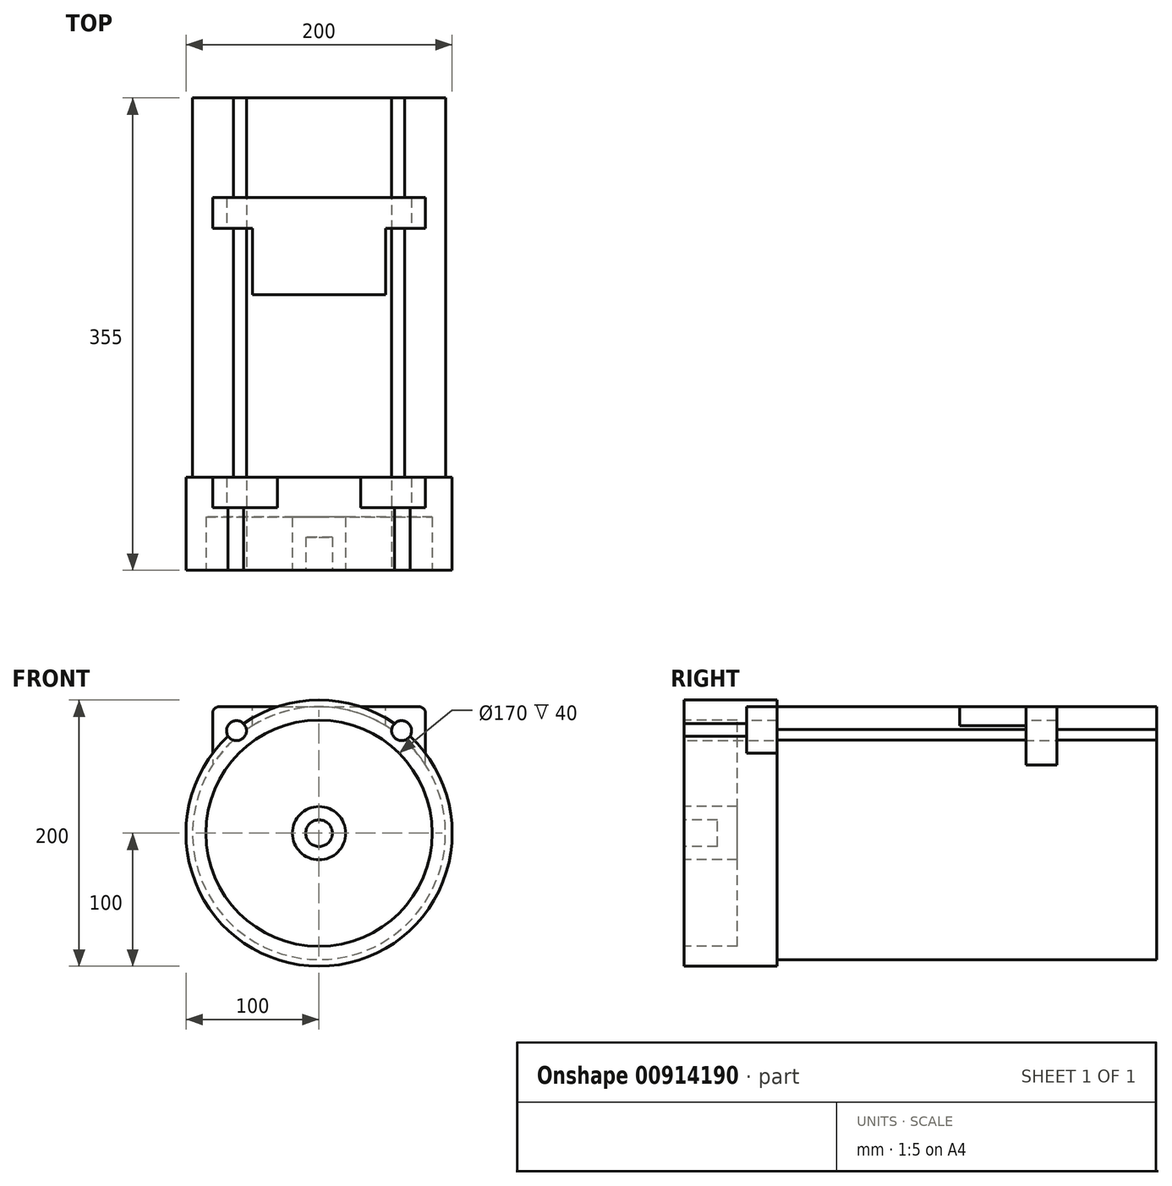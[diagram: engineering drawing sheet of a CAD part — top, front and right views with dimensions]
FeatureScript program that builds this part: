
annotation { "Feature Type Name" : "Feature", "Feature Type Description" : "" }
export const myFeature = defineFeature(function(context is Context, id is Id, definition is map)
    precondition{}
    {
        {
            var Q0;
            Q0=qCreatedBy(makeId("Front.planeOp"),FACE);
            var sketch = newSketch(context, id + "F0", { "sketchPlane" : qUnion([Q0])});
            skCircle(sketch, "E0", {"center": v(0, 0) * mm, "radius": 95 * mm});
            skSolve(sketch);
        }
        {
            var Q0;
            Q0 = qSketchRegion(id + "F0", true);
            extrude(context, id + "F1", {"entities" : qUnion([Q0]), "depth" : 355 * mm, "offsetDistance" : 25 * mm});
        }
        {
            var Q0;
            Q0=makeQuery(id+"F1.opExtrude","CAP_FACE",FACE,{"disambiguationData":[OSD([sQuery(id+"F0.wireOp",EDGE,"E0")])],"isStart":false});
            var sketch = newSketch(context, id + "F2", { "sketchPlane" : qUnion([Q0])});
            skLineSegment(sketch, "E1.top", {"start": v(80, 95) * mm, "end": v(46.44, 95) * mm});
            skPoint(sketch, "E1.middle", {"position": v(0, 0) * mm});
            skLineSegment(sketch, "E2.trimOffspring", {"start": v(-80, 50) * mm, "end": v(-80, 95) * mm});
            skLineSegment(sketch, "E3.trimOffspring", {"start": v(80, 50) * mm, "end": v(80, 95) * mm});
            skLineSegment(sketch, "E4.trimOffspring", {"start": v(-46.44, 95) * mm, "end": v(-80, 95) * mm});
            skLineSegment(sketch, "E5", {"start": v(-80, 50) * mm, "end": v(80, 50) * mm});
            skLineSegment(sketch, "E6", {"start": v(-46.44, 95) * mm, "end": v(46.44, 95) * mm});
            skLineSegment(sketch, "E7", {"start": v(0, 0) * mm, "end": v(0, 50) * mm, "construction": true});
            skSolve(sketch);
        }
        {
            var Q0;
            Q0 = qSketchRegion(id + "F2", true);
            extrude(context, id + "F3", {"entities" : qUnion([Q0]), "operationType" : NewBodyOperationType.ADD, "oppositeDirection" : true, "depth" : 70 * mm, "offsetDistance" : 25 * mm});
        }
        {
            var Q0;
            Q0=makeQuery(id+"F3.boolean.opBoolean","MERGE",FACE,{"derivedFrom":[makeQuery(id+"F1.opExtrude","CAP_FACE",FACE,{"disambiguationData":[OSD([sQuery(id+"F0.wireOp",EDGE,"E0")])],"isStart":false}),makeQuery(id+"F3.opExtrude","CAP_FACE",FACE,{"disambiguationData":[OSD([sQuery(id+"F2.wireOp",EDGE,"lusTuei3-iRUz-YuGS-ICs9-9Co0ldXmLETs"),sQuery(id+"F2.wireOp",EDGE,"E1.bottom"),sQuery(id+"F2.wireOp",EDGE,"E1.top"),sQuery(id+"F2.wireOp",EDGE,"E1.left"),sQuery(id+"F2.wireOp",EDGE,"E1.right"),sQuery(id+"F2.wireOp",EDGE,"226f6c96-94c5-4a05-a829-39864204098a.trimOffspring"),sQuery(id+"F2.wireOp",EDGE,"b6210ef0-624a-4716-9d17-52c4b066af3b.trimOffspring"),sQuery(id+"F2.wireOp",EDGE,"a472ba7a-83c2-47c1-b5ba-f65e10f710ef.trimOffspring"),sQuery(id+"F2.wireOp",EDGE,"E2.trimOffspring"),sQuery(id+"F2.wireOp",EDGE,"E3.trimOffspring"),sQuery(id+"F2.wireOp",EDGE,"E4.trimOffspring"),sQuery(id+"F2.wireOp",EDGE,"4b05afef-a105-4b7d-babe-68159069cd75.trimOffspring")])],"isStart":true})]});
            var sketch = newSketch(context, id + "F4", { "sketchPlane" : qUnion([Q0])});
            skCircle(sketch, "E8", {"center": v(0, 0) * mm, "radius": 85 * mm});
            skCircle(sketch, "E9", {"center": v(0, 0) * mm, "radius": 20 * mm});
            skSolve(sketch);
        }
        {
            var Q0;
            Q0=makeQuery(id+"F4.imprint","IMPRINT",FACE,{"disambiguationData":[TD([[makeQuery(id+"F4.imprint","IMPRINT",EDGE,{"derivedFrom":sQuery(id+"F4.wireOp",EDGE,"E8")}),1.0]])]});
            extrude(context, id + "F5", {"entities" : qUnion([Q0]), "operationType" : NewBodyOperationType.REMOVE, "oppositeDirection" : true, "depth" : 40 * mm, "offsetDistance" : 25 * mm});
        }
        {
            var Q0;
            Q0=makeQuery(id+"F5.boolean.opBoolean","SPLIT",FACE,{"disambiguationData":[TD([makeQuery(id+"F5.opExtrude","SWEPT_FACE",FACE,{"disambiguationData":[OSD([sQuery(id+"F4.wireOp",EDGE,"E9")])]})])],"derivedFrom":makeQuery(id+"F3.boolean.opBoolean","MERGE",FACE,{"derivedFrom":[makeQuery(id+"F1.opExtrude","CAP_FACE",FACE,{"disambiguationData":[OSD([sQuery(id+"F0.wireOp",EDGE,"E0")])],"isStart":false}),makeQuery(id+"F3.opExtrude","CAP_FACE",FACE,{"disambiguationData":[OSD([sQuery(id+"F2.wireOp",EDGE,"lusTuei3-iRUz-YuGS-ICs9-9Co0ldXmLETs"),sQuery(id+"F2.wireOp",EDGE,"E1.bottom"),sQuery(id+"F2.wireOp",EDGE,"E1.top"),sQuery(id+"F2.wireOp",EDGE,"E1.left"),sQuery(id+"F2.wireOp",EDGE,"E1.right"),sQuery(id+"F2.wireOp",EDGE,"226f6c96-94c5-4a05-a829-39864204098a.trimOffspring"),sQuery(id+"F2.wireOp",EDGE,"b6210ef0-624a-4716-9d17-52c4b066af3b.trimOffspring"),sQuery(id+"F2.wireOp",EDGE,"a472ba7a-83c2-47c1-b5ba-f65e10f710ef.trimOffspring"),sQuery(id+"F2.wireOp",EDGE,"E2.trimOffspring"),sQuery(id+"F2.wireOp",EDGE,"E3.trimOffspring"),sQuery(id+"F2.wireOp",EDGE,"E4.trimOffspring"),sQuery(id+"F2.wireOp",EDGE,"4b05afef-a105-4b7d-babe-68159069cd75.trimOffspring")])],"isStart":true})]})});
            var sketch = newSketch(context, id + "F6", { "sketchPlane" : qUnion([Q0])});
            skCircle(sketch, "E10", {"center": v(0, 0) * mm, "radius": 10 * mm});
            skSolve(sketch);
        }
        {
            var Q0;
            Q0 = qSketchRegion(id + "F6", true);
            extrude(context, id + "F7", {"entities" : qUnion([Q0]), "operationType" : NewBodyOperationType.REMOVE, "oppositeDirection" : true, "depth" : 25 * mm, "offsetDistance" : 25 * mm});
        }
        {
            var Q0;
            {var subQ0=sQuery(id+"F2.wireOp",EDGE,"E1.left");var subQ1=sQuery(id+"F2.wireOp",EDGE,"E1.top");var subQ2=sQuery(id+"F2.wireOp",EDGE,"E1.bottom");var subQ3=sQuery(id+"F0.wireOp",EDGE,"E0");var subQ4=sQuery(id+"F2.wireOp",EDGE,"E2.trimOffspring");var subQ5=sQuery(id+"F2.wireOp",EDGE,"E1.right");var subQ6=sQuery(id+"F2.wireOp",EDGE,"E3.trimOffspring");var subQ7=sQuery(id+"F2.wireOp",EDGE,"E4.trimOffspring");var subQ8=sQuery(id+"F2.wireOp",EDGE,"4b05afef-a105-4b7d-babe-68159069cd75.trimOffspring");Q0=makeQuery(id+"F5.boolean.opBoolean","SPLIT",FACE,{"disambiguationData":[TD([makeQuery(id+"F1.opExtrude","SWEPT_FACE",FACE,{"disambiguationData":[OSD([subQ3])]})])],"derivedFrom":makeQuery(id+"F3.boolean.opBoolean","MERGE",FACE,{"derivedFrom":[makeQuery(id+"F1.opExtrude","CAP_FACE",FACE,{"disambiguationData":[OSD([subQ3])],"isStart":false}),makeQuery(id+"F3.opExtrude","CAP_FACE",FACE,{"disambiguationData":[OSD([sQuery(id+"F2.wireOp",EDGE,"lusTuei3-iRUz-YuGS-ICs9-9Co0ldXmLETs"),subQ2,subQ1,subQ0,subQ5,sQuery(id+"F2.wireOp",EDGE,"226f6c96-94c5-4a05-a829-39864204098a.trimOffspring"),sQuery(id+"F2.wireOp",EDGE,"b6210ef0-624a-4716-9d17-52c4b066af3b.trimOffspring"),sQuery(id+"F2.wireOp",EDGE,"a472ba7a-83c2-47c1-b5ba-f65e10f710ef.trimOffspring"),subQ4,subQ6,subQ7,subQ8])],"isStart":true})]})});}
            var sketch = newSketch(context, id + "F8", { "sketchPlane" : qUnion([Q0])});
            skCircle(sketch, "E11", {"center": v(-62, 77) * mm, "radius": 7.5 * mm});
            skCircle(sketch, "E12.3.0", {"center": v(62, 77) * mm, "radius": 7.5 * mm});
            skPoint(sketch, "E12.center", {"position": v(0, 15) * mm});
            skSolve(sketch);
        }
        {
            var Q0;
            Q0=makeQuery(id+"F2zg9YKfClmn7O4_1.1.F3.boolean.opBoolean","MERGE",FACE,{"derivedFrom":[makeQuery(id+"F1.opExtrude","CAP_FACE",FACE,{"disambiguationData":[OSD([sQuery(id+"F0.wireOp",EDGE,"E0")])],"isStart":true}),makeQuery(id+"F2zg9YKfClmn7O4_1.1.F3.opExtrude","CAP_FACE",FACE,{"disambiguationData":[OSD([sQuery(id+"F2.wireOp",EDGE,"E1.top"),sQuery(id+"F2.wireOp",EDGE,"E2.trimOffspring"),sQuery(id+"F2.wireOp",EDGE,"E3.trimOffspring"),sQuery(id+"F2.wireOp",EDGE,"E4.trimOffspring"),sQuery(id+"F2.wireOp",EDGE,"E5"),sQuery(id+"F2.wireOp",EDGE,"E6")])],"isStart":true})]});
            var sketch = newSketch(context, id + "F9", { "sketchPlane" : qUnion([Q0])});
            skArc(sketch, "E13", {"start": v(80, 51.23) * mm, "mid": v(0, 95) * mm, "end": v(-80, 51.23) * mm});
            skLineSegment(sketch, "E14", {"start": v(-80, 51.23) * mm, "end": v(-80, 90) * mm});
            skLineSegment(sketch, "E15", {"start": v(-75, 95) * mm, "end": v(75, 95) * mm});
            skLineSegment(sketch, "E16", {"start": v(80, 90) * mm, "end": v(80, 51.23) * mm});
            skLineSegment(sketch, "E17", {"start": v(0, 95) * mm, "end": v(0, 0) * mm, "construction": true});
            skPoint(sketch, "E18.visualSharp", {"position": v(-80, 95) * mm});
            skArc(sketch, "E18.filletArc", {"start": v(-75, 95) * mm, "mid": v(-78.54, 93.54) * mm, "end": v(-80, 90) * mm});
            skPoint(sketch, "E19.visualSharp", {"position": v(80, 95) * mm});
            skArc(sketch, "E19.filletArc", {"start": v(80, 90) * mm, "mid": v(78.54, 93.54) * mm, "end": v(75, 95) * mm});
            skSolve(sketch);
        }
        {
            var Q0;
            Q0 = qSketchRegion(id + "F9", true);
            extrude(context, id + "F10", {"entities" : qUnion([Q0]), "operationType" : NewBodyOperationType.ADD, "oppositeDirection" : true, "depth" : 98 * mm, "offsetDistance" : 25 * mm});
        }
        {
            var Q0;
            {var subQ0=sQuery(id+"F2.wireOp",EDGE,"E6");var subQ1=sQuery(id+"F2.wireOp",EDGE,"E4.trimOffspring");var subQ2=sQuery(id+"F2.wireOp",EDGE,"E1.top");var subQ3=sQuery(id+"F2.wireOp",EDGE,"E3.trimOffspring");var subQ4=makeQuery(id+"F3.opExtrude","CAP_FACE",FACE,{"disambiguationData":[OSD([subQ2,sQuery(id+"F2.wireOp",EDGE,"E2.trimOffspring"),subQ3,subQ1,sQuery(id+"F2.wireOp",EDGE,"E5"),subQ0])],"isStart":false});Q0=makeQuery(id+"F3.boolean.opBoolean","SPLIT",FACE,{"disambiguationData":[TD([makeQuery(id+"F3.opExtrude","SWEPT_FACE",FACE,{"disambiguationData":[OSD([subQ3])]})])],"derivedFrom":subQ4});}
            var sketch = newSketch(context, id + "F11", { "sketchPlane" : qUnion([Q0])});
            skCircle(sketch, "E20", {"center": v(0, 0) * mm, "radius": 100 * mm});
            skCircle(sketch, "E21", {"center": v(0, 0) * mm, "radius": 95 * mm});
            skSolve(sketch);
        }
        {
            var Q0;
            Q0 = qSketchRegion(id + "F11", true);
            extrude(context, id + "F12", {"entities" : qUnion([Q0]), "operationType" : NewBodyOperationType.ADD, "oppositeDirection" : true, "depth" : 70 * mm, "offsetDistance" : 25 * mm});
        }
        {
            var Q0;
            Q0=makeQuery(id+"F8.imprint","IMPRINT",FACE,{"disambiguationData":[TD([[makeQuery(id+"F8.imprint","IMPRINT",EDGE,{"derivedFrom":sQuery(id+"F8.wireOp",EDGE,"E11")}),1.0]])]});
            var Q1;
            Q1=makeQuery(id+"F8.imprint","IMPRINT",FACE,{"disambiguationData":[TD([[makeQuery(id+"F8.imprint","IMPRINT",EDGE,{"derivedFrom":sQuery(id+"F8.wireOp",EDGE,"E12.3.0")}),1.0]])]});
            var Q2;
            Q2=makeQuery(id+"F8.imprint","IMPRINT",FACE,{"disambiguationData":[TD([[makeQuery(id+"F8.imprint","IMPRINT",EDGE,{"derivedFrom":sQuery(id+"F8.wireOp",EDGE,"E12.2.0")}),1.0]])]});
            var Q3;
            Q3=makeQuery(id+"F8.imprint","IMPRINT",FACE,{"disambiguationData":[TD([[makeQuery(id+"F8.imprint","IMPRINT",EDGE,{"derivedFrom":sQuery(id+"F8.wireOp",EDGE,"E12.1.0")}),1.0]])]});
            extrude(context, id + "F13", {"entities" : qUnion([Q0, Q1, Q2, Q3]), "operationType" : NewBodyOperationType.REMOVE, "oppositeDirection" : true, "depth" : 500 * mm, "offsetDistance" : 25 * mm});
        }
        {
            var Q0;
            Q0=makeQuery(id+"F2zg9YKfClmn7O4_1.1.F3.opExtrude","SWEPT_EDGE",EDGE,{"disambiguationData":[OSD([sQuery(id+"F2.wireOp",EDGE,"E2.trimOffspring"),sQuery(id+"F2.wireOp",EDGE,"E4.trimOffspring")])]});
            var Q1;
            Q1=makeQuery(id+"F2zg9YKfClmn7O4_1.1.F3.opExtrude","SWEPT_EDGE",EDGE,{"disambiguationData":[OSD([sQuery(id+"F2.wireOp",EDGE,"E1.top"),sQuery(id+"F2.wireOp",EDGE,"E3.trimOffspring")])]});
            var Q2;
            Q2=makeQuery(id+"F3.opExtrude","SWEPT_EDGE",EDGE,{"disambiguationData":[OSD([sQuery(id+"F2.wireOp",EDGE,"E2.trimOffspring"),sQuery(id+"F2.wireOp",EDGE,"E4.trimOffspring")])]});
            var Q3;
            Q3=makeQuery(id+"F3.opExtrude","SWEPT_EDGE",EDGE,{"disambiguationData":[OSD([sQuery(id+"F2.wireOp",EDGE,"E1.top"),sQuery(id+"F2.wireOp",EDGE,"E3.trimOffspring")])]});
            var Q4;
            Q4=makeQuery(id+"F2zg9YKfClmn7O4_1.1.F3.opExtrude","SWEPT_EDGE",EDGE,{"disambiguationData":[OSD([sQuery(id+"F2.wireOp",EDGE,"E1.right"),sQuery(id+"F2.wireOp",EDGE,"4b05afef-a105-4b7d-babe-68159069cd75.trimOffspring")])]});
            var Q5;
            Q5=makeQuery(id+"F3.opExtrude","SWEPT_EDGE",EDGE,{"disambiguationData":[OSD([sQuery(id+"F2.wireOp",EDGE,"E1.right"),sQuery(id+"F2.wireOp",EDGE,"4b05afef-a105-4b7d-babe-68159069cd75.trimOffspring")])]});
            var Q6;
            Q6=makeQuery(id+"F2zg9YKfClmn7O4_1.1.F3.opExtrude","CAP_EDGE",EDGE,{"disambiguationData":[OSD([sQuery(id+"F2.wireOp",EDGE,"E1.bottom")])],"isStart":true});
            var Q7;
            Q7=makeQuery(id+"F3.opExtrude","SWEPT_EDGE",EDGE,{"disambiguationData":[OSD([sQuery(id+"F2.wireOp",EDGE,"E1.bottom"),sQuery(id+"F2.wireOp",EDGE,"E1.left")])]});
            fillet(context, id + "F14", {"entities" : qUnion([Q0, Q1, Q2, Q3, Q4, Q5, Q6, Q7]), "radius" : 5 * mm, "tangentPropagation" : true, "allowEdgeOverflow" : false});
        }
        {
            var Q0;
            {var subQ0=sQuery(id+"F2.wireOp",EDGE,"E3.trimOffspring");var subQ1=sQuery(id+"F2.wireOp",EDGE,"E2.trimOffspring");var subQ2=sQuery(id+"F2.wireOp",EDGE,"E6");var subQ3=sQuery(id+"F2.wireOp",EDGE,"E4.trimOffspring");var subQ4=sQuery(id+"F2.wireOp",EDGE,"E1.top");var subQ5=sQuery(id+"F0.wireOp",EDGE,"E0");Q0=makeQuery(id+"F5.boolean.opBoolean","SPLIT",FACE,{"disambiguationData":[TD([makeQuery(id+"F1.opExtrude","SWEPT_FACE",FACE,{"disambiguationData":[OSD([subQ5])]})])],"derivedFrom":makeQuery(id+"F3.boolean.opBoolean","MERGE",FACE,{"derivedFrom":[makeQuery(id+"F1.opExtrude","CAP_FACE",FACE,{"disambiguationData":[OSD([subQ5])],"isStart":false}),makeQuery(id+"F3.opExtrude","CAP_FACE",FACE,{"disambiguationData":[OSD([subQ4,subQ1,subQ0,subQ3,sQuery(id+"F2.wireOp",EDGE,"E5"),subQ2])],"isStart":true})]})});}
            var sketch = newSketch(context, id + "F15", { "sketchPlane" : qUnion([Q0])});
            skArc(sketch, "E22", {"start": v(80, 60) * mm, "mid": v(0, 100) * mm, "end": v(-80, 60) * mm});
            skLineSegment(sketch, "E23", {"start": v(-80, 60) * mm, "end": v(-80, 108.73) * mm});
            skLineSegment(sketch, "E24", {"start": v(-80, 108.73) * mm, "end": v(80, 108.73) * mm});
            skPoint(sketch, "E24.endSnap0", {"position": v(80, 102.32) * mm});
            skLineSegment(sketch, "E25", {"start": v(80, 108.73) * mm, "end": v(80, 60) * mm});
            skSolve(sketch);
        }
        {
            var Q0;
            Q0 = qSketchRegion(id + "F15", true);
            extrude(context, id + "F16", {"entities" : qUnion([Q0]), "operationType" : NewBodyOperationType.REMOVE, "oppositeDirection" : true, "depth" : 47 * mm, "offsetDistance" : 25 * mm});
        }
        {
            var Q0;
            {var subQ0=sQuery(id+"F9.wireOp",EDGE,"E15");var subQ1=sQuery(id+"F9.wireOp",EDGE,"E13");Q0=makeQuery(id+"F10.boolean.opBoolean","MERGE",FACE,{"derivedFrom":[makeQuery(id+"F1.opExtrude","CAP_FACE",FACE,{"disambiguationData":[OSD([sQuery(id+"F0.wireOp",EDGE,"E0")])],"isStart":true}),makeQuery(id+"F10.opExtrude","CAP_FACE",FACE,{"disambiguationData":[OSD([subQ1,subQ0,sQuery(id+"F9.wireOp",EDGE,"E16"),sQuery(id+"F9.wireOp",EDGE,"E19.filletArc")])],"isStart":true}),makeQuery(id+"F10.opExtrude","CAP_FACE",FACE,{"disambiguationData":[OSD([subQ1,sQuery(id+"F9.wireOp",EDGE,"E14"),subQ0,sQuery(id+"F9.wireOp",EDGE,"E18.filletArc")])],"isStart":true})]});}
            var sketch = newSketch(context, id + "F17", { "sketchPlane" : qUnion([Q0])});
            skArc(sketch, "E26", {"start": v(80, 51.23) * mm, "mid": v(0, 95) * mm, "end": v(-80, 51.23) * mm});
            skLineSegment(sketch, "E27", {"start": v(-80, 51.23) * mm, "end": v(-80, 103.6) * mm});
            skLineSegment(sketch, "E28", {"start": v(-80, 103.6) * mm, "end": v(80, 103.6) * mm});
            skLineSegment(sketch, "E29", {"start": v(80, 103.6) * mm, "end": v(80, 51.23) * mm});
            skSolve(sketch);
        }
        {
            var Q0;
            Q0 = qSketchRegion(id + "F17", true);
            extrude(context, id + "F18", {"entities" : qUnion([Q0]), "operationType" : NewBodyOperationType.REMOVE, "oppositeDirection" : true, "depth" : 75 * mm, "offsetDistance" : 25 * mm});
        }
        {
            var Q0;
            {var subQ0=sQuery(id+"F9.wireOp",EDGE,"E15");Q0=makeQuery(id+"F10.boolean.opBoolean","MERGE",FACE,{"derivedFrom":[makeQuery(id+"F10.opExtrude","SWEPT_FACE",FACE,{"disambiguationData":[OSD([subQ0]),TDD([makeQuery(id+"F9.imprint","IMPRINT",EDGE,{"disambiguationData":[TD([[makeQuery(id+"F9.imprint","INTERSECT",VERTEX,{"derivedFrom":[subQ0,sQuery(id+"F9.wireOp",EDGE,"E18.filletArc")]}),-1.0]])],"derivedFrom":subQ0})])]}),makeQuery(id+"F10.opExtrude","SWEPT_FACE",FACE,{"disambiguationData":[OSD([subQ0]),TDD([makeQuery(id+"F9.imprint","IMPRINT",EDGE,{"disambiguationData":[TD([[makeQuery(id+"F9.imprint","INTERSECT",VERTEX,{"derivedFrom":[subQ0,sQuery(id+"F9.wireOp",EDGE,"E19.filletArc")]}),1.0]])],"derivedFrom":subQ0})])]})]});}
            var sketch = newSketch(context, id + "F19", { "sketchPlane" : qUnion([Q0])});
            skLineSegment(sketch, "E30.bottom", {"start": v(-50, -98) * mm, "end": v(50, -98) * mm});
            skLineSegment(sketch, "E30.top", {"start": v(-50, -148) * mm, "end": v(50, -148) * mm});
            skLineSegment(sketch, "E30.left", {"start": v(-50, -98) * mm, "end": v(-50, -148) * mm});
            skLineSegment(sketch, "E30.right", {"start": v(50, -98) * mm, "end": v(50, -148) * mm});
            skSolve(sketch);
        }
        {
            var Q0;
            Q0 = qSketchRegion(id + "F19", true);
            extrude(context, id + "F20", {"entities" : qUnion([Q0]), "operationType" : NewBodyOperationType.ADD, "oppositeDirection" : true, "depth" : 22 * mm, "offsetDistance" : 25 * mm});
        }
    });
